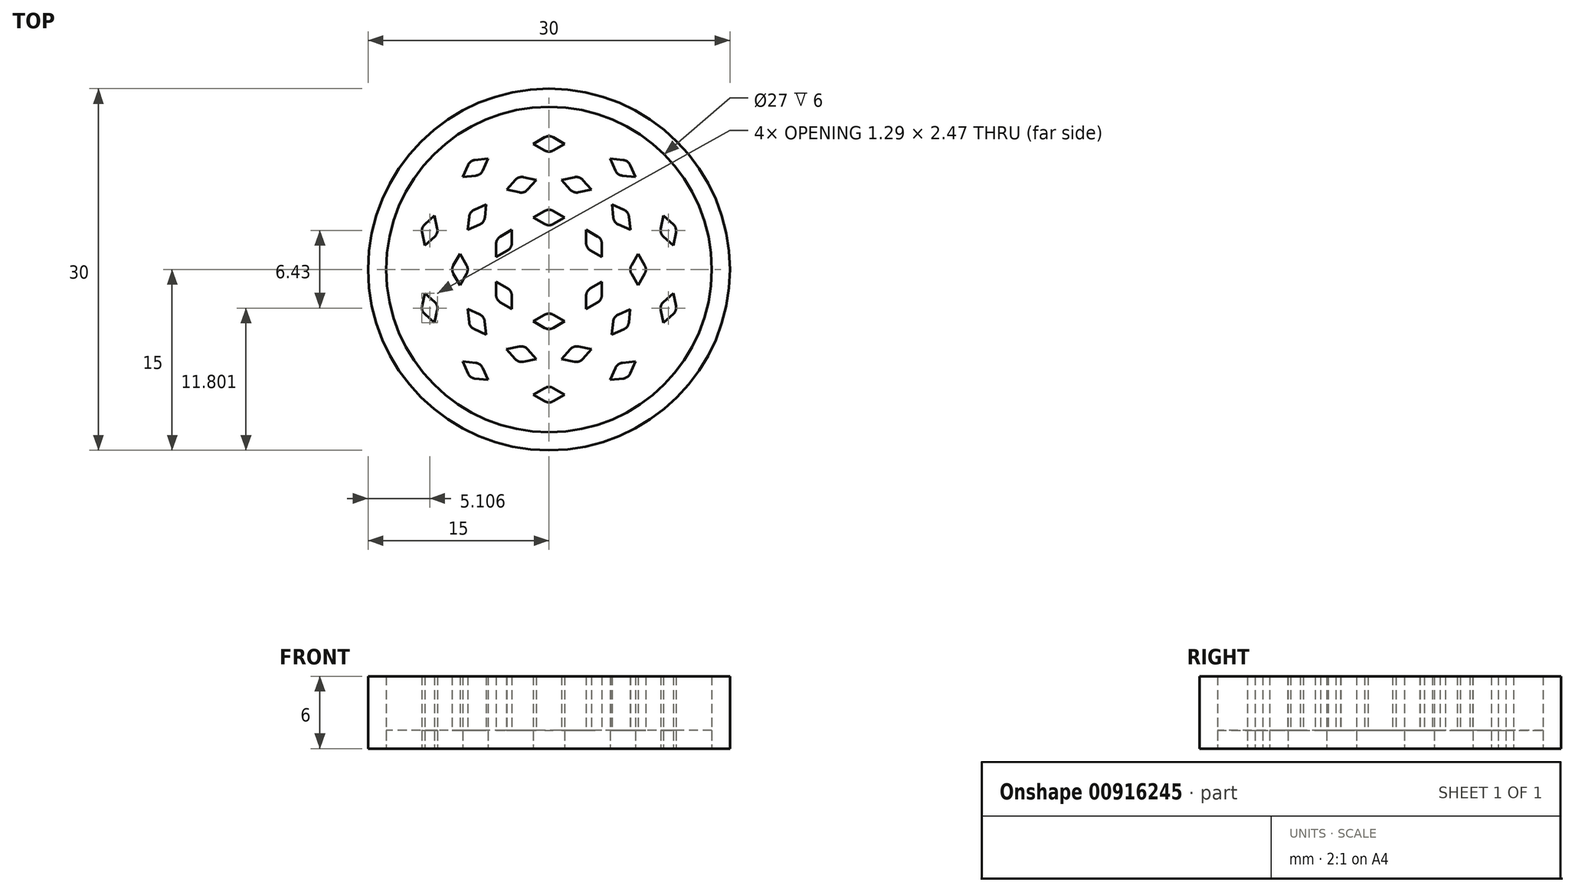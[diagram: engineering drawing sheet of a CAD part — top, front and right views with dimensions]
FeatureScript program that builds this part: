
annotation { "Feature Type Name" : "Feature", "Feature Type Description" : "" }
export const myFeature = defineFeature(function(context is Context, id is Id, definition is map)
    precondition{}
    {
        {
            var Q0;
            Q0=qCreatedBy(makeId("Top.planeOp"),FACE);
            var sketch = newSketch(context, id + "F0", { "sketchPlane" : qUnion([Q0])});
            skCircle(sketch, "E0", {"center": v(0, 0) * mm, "radius": 15 * mm});
            skCircle(sketch, "E1.0", {"center": v(0, 0) * mm, "radius": 13.5 * mm});
            skCircle(sketch, "E2.0", {"center": v(0, 0) * mm, "radius": 10.5 * mm, "construction": true});
            skCircle(sketch, "E3.0", {"center": v(0, 0) * mm, "radius": 7.5 * mm, "construction": true});
            skCircle(sketch, "E4.0", {"center": v(0, 0) * mm, "radius": 4.5 * mm, "construction": true});
            skLineSegment(sketch, "E5", {"start": v(0, 10.5) * mm, "end": v(0, 10.5) * mm});
            skLineSegment(sketch, "E6", {"start": v(0, 18.88) * mm, "end": v(0, 0) * mm, "construction": true});
            skLineSegment(sketch, "E7", {"start": v(-0.35, 10.97) * mm, "end": v(-1.3, 10.42) * mm});
            skLineSegment(sketch, "E8", {"start": v(0.35, 10.97) * mm, "end": v(1.3, 10.42) * mm});
            skPoint(sketch, "E9.visualSharp", {"position": v(0, 11.17) * mm});
            skArc(sketch, "E9.filletArc", {"start": v(0.35, 10.97) * mm, "mid": v(0, 11.06) * mm, "end": v(-0.35, 10.97) * mm});
            skLineSegment(sketch, "E10", {"start": v(-1.3, 10.42) * mm, "end": v(-0.35, 9.87) * mm});
            skLineSegment(sketch, "E11", {"start": v(0.35, 9.87) * mm, "end": v(1.3, 10.42) * mm});
            skPoint(sketch, "E12.visualSharp", {"position": v(0, 9.67) * mm});
            skArc(sketch, "E12.filletArc", {"start": v(-0.35, 9.87) * mm, "mid": v(0, 9.78) * mm, "end": v(0.35, 9.87) * mm});
            skLineSegment(sketch, "E13.1.1", {"start": v(-7.17, 7.67) * mm, "end": v(-6.08, 7.78) * mm});
            skLineSegment(sketch, "E13.1.2", {"start": v(-6.72, 8.67) * mm, "end": v(-7.17, 7.67) * mm});
            skArc(sketch, "E13.1.3", {"start": v(-6.15, 9.08) * mm, "mid": v(-6.5, 8.95) * mm, "end": v(-6.72, 8.67) * mm});
            skLineSegment(sketch, "E13.1.4", {"start": v(-6.15, 9.08) * mm, "end": v(-5.06, 9.2) * mm});
            skLineSegment(sketch, "E13.1.5", {"start": v(-5.5, 8.2) * mm, "end": v(-5.06, 9.2) * mm});
            skArc(sketch, "E13.1.6", {"start": v(-6.08, 7.78) * mm, "mid": v(-5.74, 7.91) * mm, "end": v(-5.5, 8.2) * mm});
            skCircle(sketch, "E13.2.0", {"center": v(0.02, 0.01) * mm, "radius": 10.5 * mm, "construction": true});
            skLineSegment(sketch, "E13.2.1", {"start": v(-10.3, 2) * mm, "end": v(-9.48, 2.73) * mm});
            skLineSegment(sketch, "E13.2.2", {"start": v(-10.52, 3.07) * mm, "end": v(-10.3, 2) * mm});
            skArc(sketch, "E13.2.3", {"start": v(-10.3, 3.73) * mm, "mid": v(-10.5, 3.43) * mm, "end": v(-10.52, 3.07) * mm});
            skLineSegment(sketch, "E13.2.4", {"start": v(-10.3, 3.73) * mm, "end": v(-9.5, 4.47) * mm});
            skLineSegment(sketch, "E13.2.5", {"start": v(-9.26, 3.4) * mm, "end": v(-9.5, 4.47) * mm});
            skArc(sketch, "E13.2.6", {"start": v(-9.48, 2.73) * mm, "mid": v(-9.28, 3.03) * mm, "end": v(-9.26, 3.4) * mm});
            skCircle(sketch, "E13.3.0", {"center": v(0.02, 0.02) * mm, "radius": 10.5 * mm, "construction": true});
            skLineSegment(sketch, "E13.3.1", {"start": v(-9.5, -4.43) * mm, "end": v(-9.26, -3.36) * mm});
            skLineSegment(sketch, "E13.3.2", {"start": v(-10.3, -3.7) * mm, "end": v(-9.5, -4.43) * mm});
            skArc(sketch, "E13.3.3", {"start": v(-10.52, -3.04) * mm, "mid": v(-10.5, -3.4) * mm, "end": v(-10.3, -3.7) * mm});
            skLineSegment(sketch, "E13.3.4", {"start": v(-10.52, -3.04) * mm, "end": v(-10.3, -1.96) * mm});
            skLineSegment(sketch, "E13.3.5", {"start": v(-9.48, -2.7) * mm, "end": v(-10.3, -1.96) * mm});
            skArc(sketch, "E13.3.6", {"start": v(-9.26, -3.36) * mm, "mid": v(-9.28, -3) * mm, "end": v(-9.48, -2.7) * mm});
            skCircle(sketch, "E13.4.0", {"center": v(0, 0.03) * mm, "radius": 10.5 * mm, "construction": true});
            skLineSegment(sketch, "E13.4.1", {"start": v(-5.06, -9.16) * mm, "end": v(-5.5, -8.16) * mm});
            skLineSegment(sketch, "E13.4.2", {"start": v(-6.15, -9.05) * mm, "end": v(-5.06, -9.16) * mm});
            skArc(sketch, "E13.4.3", {"start": v(-6.72, -8.64) * mm, "mid": v(-6.5, -8.92) * mm, "end": v(-6.15, -9.05) * mm});
            skLineSegment(sketch, "E13.4.4", {"start": v(-6.72, -8.64) * mm, "end": v(-7.17, -7.64) * mm});
            skLineSegment(sketch, "E13.4.5", {"start": v(-6.08, -7.75) * mm, "end": v(-7.17, -7.64) * mm});
            skArc(sketch, "E13.4.6", {"start": v(-5.5, -8.16) * mm, "mid": v(-5.74, -7.88) * mm, "end": v(-6.08, -7.75) * mm});
            skCircle(sketch, "E13.5.0", {"center": v(0, 0.03) * mm, "radius": 10.5 * mm, "construction": true});
            skLineSegment(sketch, "E13.5.1", {"start": v(1.3, -10.39) * mm, "end": v(0.35, -9.84) * mm});
            skLineSegment(sketch, "E13.5.2", {"start": v(0.35, -10.94) * mm, "end": v(1.3, -10.39) * mm});
            skArc(sketch, "E13.5.3", {"start": v(-0.35, -10.94) * mm, "mid": v(0, -11.03) * mm, "end": v(0.35, -10.94) * mm});
            skLineSegment(sketch, "E13.5.4", {"start": v(-0.35, -10.94) * mm, "end": v(-1.3, -10.39) * mm});
            skLineSegment(sketch, "E13.5.5", {"start": v(-0.35, -9.84) * mm, "end": v(-1.3, -10.39) * mm});
            skArc(sketch, "E13.5.6", {"start": v(0.35, -9.84) * mm, "mid": v(0, -9.75) * mm, "end": v(-0.35, -9.84) * mm});
            skCircle(sketch, "E13.6.0", {"center": v(0, 0.03) * mm, "radius": 10.5 * mm, "construction": true});
            skLineSegment(sketch, "E13.6.1", {"start": v(7.17, -7.64) * mm, "end": v(6.08, -7.75) * mm});
            skLineSegment(sketch, "E13.6.2", {"start": v(6.72, -8.64) * mm, "end": v(7.17, -7.64) * mm});
            skArc(sketch, "E13.6.3", {"start": v(6.15, -9.05) * mm, "mid": v(6.5, -8.92) * mm, "end": v(6.72, -8.64) * mm});
            skLineSegment(sketch, "E13.6.4", {"start": v(6.15, -9.05) * mm, "end": v(5.06, -9.16) * mm});
            skLineSegment(sketch, "E13.6.5", {"start": v(5.5, -8.16) * mm, "end": v(5.06, -9.16) * mm});
            skArc(sketch, "E13.6.6", {"start": v(6.08, -7.75) * mm, "mid": v(5.74, -7.88) * mm, "end": v(5.5, -8.16) * mm});
            skCircle(sketch, "E13.7.0", {"center": v(-0.02, 0.02) * mm, "radius": 10.5 * mm, "construction": true});
            skLineSegment(sketch, "E13.7.1", {"start": v(10.3, -1.96) * mm, "end": v(9.48, -2.7) * mm});
            skLineSegment(sketch, "E13.7.2", {"start": v(10.52, -3.04) * mm, "end": v(10.3, -1.96) * mm});
            skArc(sketch, "E13.7.3", {"start": v(10.3, -3.7) * mm, "mid": v(10.5, -3.4) * mm, "end": v(10.52, -3.04) * mm});
            skLineSegment(sketch, "E13.7.4", {"start": v(10.3, -3.7) * mm, "end": v(9.5, -4.43) * mm});
            skLineSegment(sketch, "E13.7.5", {"start": v(9.26, -3.36) * mm, "end": v(9.5, -4.43) * mm});
            skArc(sketch, "E13.7.6", {"start": v(9.48, -2.7) * mm, "mid": v(9.28, -3) * mm, "end": v(9.26, -3.36) * mm});
            skCircle(sketch, "E13.8.0", {"center": v(-0.02, 0.01) * mm, "radius": 10.5 * mm, "construction": true});
            skLineSegment(sketch, "E13.8.1", {"start": v(9.5, 4.47) * mm, "end": v(9.26, 3.4) * mm});
            skLineSegment(sketch, "E13.8.2", {"start": v(10.3, 3.73) * mm, "end": v(9.5, 4.47) * mm});
            skArc(sketch, "E13.8.3", {"start": v(10.52, 3.07) * mm, "mid": v(10.5, 3.43) * mm, "end": v(10.3, 3.73) * mm});
            skLineSegment(sketch, "E13.8.4", {"start": v(10.52, 3.07) * mm, "end": v(10.3, 2) * mm});
            skLineSegment(sketch, "E13.8.5", {"start": v(9.48, 2.73) * mm, "end": v(10.3, 2) * mm});
            skArc(sketch, "E13.8.6", {"start": v(9.26, 3.4) * mm, "mid": v(9.28, 3.03) * mm, "end": v(9.48, 2.73) * mm});
            skLineSegment(sketch, "E13.9.1", {"start": v(5.06, 9.2) * mm, "end": v(5.5, 8.2) * mm});
            skLineSegment(sketch, "E13.9.2", {"start": v(6.15, 9.08) * mm, "end": v(5.06, 9.2) * mm});
            skArc(sketch, "E13.9.3", {"start": v(6.72, 8.67) * mm, "mid": v(6.5, 8.95) * mm, "end": v(6.15, 9.08) * mm});
            skLineSegment(sketch, "E13.9.4", {"start": v(6.72, 8.67) * mm, "end": v(7.17, 7.67) * mm});
            skLineSegment(sketch, "E13.9.5", {"start": v(6.08, 7.78) * mm, "end": v(7.17, 7.67) * mm});
            skArc(sketch, "E13.9.6", {"start": v(5.5, 8.2) * mm, "mid": v(5.74, 7.91) * mm, "end": v(6.08, 7.78) * mm});
            skPoint(sketch, "E13.center", {"position": v(0, 0.02) * mm});
            skLineSegment(sketch, "E14", {"start": v(-1.3, 10.42) * mm, "end": v(-5.06, 9.2) * mm, "construction": true});
            skLineSegment(sketch, "E15", {"start": v(-3.18, 9.8) * mm, "end": v(-2.31, 7.13) * mm, "construction": true});
            skLineSegment(sketch, "E16", {"start": v(-3.51, 6.63) * mm, "end": v(-2.78, 7.44) * mm});
            skLineSegment(sketch, "E17", {"start": v(-2.11, 7.66) * mm, "end": v(-1.04, 7.43) * mm});
            skLineSegment(sketch, "E18", {"start": v(-1.04, 7.43) * mm, "end": v(-1.78, 6.61) * mm});
            skLineSegment(sketch, "E19", {"start": v(-2.44, 6.4) * mm, "end": v(-3.51, 6.63) * mm});
            skPoint(sketch, "E20.visualSharp", {"position": v(-2.5, 7.74) * mm});
            skArc(sketch, "E20.filletArc", {"start": v(-2.11, 7.66) * mm, "mid": v(-2.48, 7.64) * mm, "end": v(-2.78, 7.44) * mm});
            skPoint(sketch, "E21.visualSharp", {"position": v(-2.05, 6.31) * mm});
            skArc(sketch, "E21.filletArc", {"start": v(-2.44, 6.4) * mm, "mid": v(-2.08, 6.42) * mm, "end": v(-1.78, 6.61) * mm});
            skLineSegment(sketch, "E22.1.1", {"start": v(-6.21, 4.95) * mm, "end": v(-5.2, 5.4) * mm});
            skArc(sketch, "E22.1.2", {"start": v(-6.21, 4.95) * mm, "mid": v(-6.5, 4.72) * mm, "end": v(-6.62, 4.38) * mm});
            skLineSegment(sketch, "E22.1.3", {"start": v(-6.74, 3.3) * mm, "end": v(-6.62, 4.38) * mm});
            skLineSegment(sketch, "E22.1.4", {"start": v(-5.74, 3.74) * mm, "end": v(-6.74, 3.3) * mm});
            skArc(sketch, "E22.1.5", {"start": v(-5.74, 3.74) * mm, "mid": v(-5.45, 3.97) * mm, "end": v(-5.32, 4.3) * mm});
            skLineSegment(sketch, "E22.1.6", {"start": v(-5.2, 5.4) * mm, "end": v(-5.32, 4.3) * mm});
            skLineSegment(sketch, "E22.2.1", {"start": v(-7.93, 0.35) * mm, "end": v(-7.39, 1.3) * mm});
            skArc(sketch, "E22.2.2", {"start": v(-7.93, 0.35) * mm, "mid": v(-8.03, 0) * mm, "end": v(-7.93, -0.35) * mm});
            skLineSegment(sketch, "E22.2.3", {"start": v(-7.39, -1.3) * mm, "end": v(-7.93, -0.35) * mm});
            skLineSegment(sketch, "E22.2.4", {"start": v(-6.84, -0.35) * mm, "end": v(-7.39, -1.3) * mm});
            skArc(sketch, "E22.2.5", {"start": v(-6.84, -0.35) * mm, "mid": v(-6.74, 0) * mm, "end": v(-6.84, 0.35) * mm});
            skLineSegment(sketch, "E22.2.6", {"start": v(-7.39, 1.3) * mm, "end": v(-6.84, 0.35) * mm});
            skLineSegment(sketch, "E22.3.1", {"start": v(-6.63, -4.38) * mm, "end": v(-6.74, -3.29) * mm});
            skArc(sketch, "E22.3.2", {"start": v(-6.63, -4.38) * mm, "mid": v(-6.5, -4.72) * mm, "end": v(-6.22, -4.94) * mm});
            skLineSegment(sketch, "E22.3.3", {"start": v(-5.22, -5.39) * mm, "end": v(-6.22, -4.94) * mm});
            skLineSegment(sketch, "E22.3.4", {"start": v(-5.33, -4.3) * mm, "end": v(-5.22, -5.39) * mm});
            skArc(sketch, "E22.3.5", {"start": v(-5.33, -4.3) * mm, "mid": v(-5.46, -3.96) * mm, "end": v(-5.74, -3.73) * mm});
            skLineSegment(sketch, "E22.3.6", {"start": v(-6.74, -3.29) * mm, "end": v(-5.74, -3.73) * mm});
            skLineSegment(sketch, "E22.4.1", {"start": v(-2.79, -7.44) * mm, "end": v(-3.52, -6.62) * mm});
            skArc(sketch, "E22.4.2", {"start": v(-2.79, -7.44) * mm, "mid": v(-2.49, -7.63) * mm, "end": v(-2.12, -7.65) * mm});
            skLineSegment(sketch, "E22.4.3", {"start": v(-1.05, -7.43) * mm, "end": v(-2.12, -7.65) * mm});
            skLineSegment(sketch, "E22.4.4", {"start": v(-1.78, -6.61) * mm, "end": v(-1.05, -7.43) * mm});
            skArc(sketch, "E22.4.5", {"start": v(-1.78, -6.61) * mm, "mid": v(-2.09, -6.41) * mm, "end": v(-2.45, -6.4) * mm});
            skLineSegment(sketch, "E22.4.6", {"start": v(-3.52, -6.62) * mm, "end": v(-2.45, -6.4) * mm});
            skLineSegment(sketch, "E22.5.1", {"start": v(2.11, -7.66) * mm, "end": v(1.04, -7.43) * mm});
            skArc(sketch, "E22.5.2", {"start": v(2.11, -7.66) * mm, "mid": v(2.48, -7.64) * mm, "end": v(2.78, -7.44) * mm});
            skLineSegment(sketch, "E22.5.3", {"start": v(3.51, -6.63) * mm, "end": v(2.78, -7.44) * mm});
            skLineSegment(sketch, "E22.5.4", {"start": v(2.44, -6.4) * mm, "end": v(3.51, -6.63) * mm});
            skArc(sketch, "E22.5.5", {"start": v(2.44, -6.4) * mm, "mid": v(2.08, -6.42) * mm, "end": v(1.78, -6.61) * mm});
            skLineSegment(sketch, "E22.5.6", {"start": v(1.04, -7.43) * mm, "end": v(1.78, -6.61) * mm});
            skLineSegment(sketch, "E22.6.1", {"start": v(6.21, -4.95) * mm, "end": v(5.2, -5.4) * mm});
            skArc(sketch, "E22.6.2", {"start": v(6.21, -4.95) * mm, "mid": v(6.5, -4.72) * mm, "end": v(6.62, -4.38) * mm});
            skLineSegment(sketch, "E22.6.3", {"start": v(6.74, -3.3) * mm, "end": v(6.62, -4.38) * mm});
            skLineSegment(sketch, "E22.6.4", {"start": v(5.74, -3.74) * mm, "end": v(6.74, -3.3) * mm});
            skArc(sketch, "E22.6.5", {"start": v(5.74, -3.74) * mm, "mid": v(5.45, -3.97) * mm, "end": v(5.32, -4.3) * mm});
            skLineSegment(sketch, "E22.6.6", {"start": v(5.2, -5.4) * mm, "end": v(5.32, -4.3) * mm});
            skLineSegment(sketch, "E22.7.1", {"start": v(7.93, -0.35) * mm, "end": v(7.39, -1.3) * mm});
            skArc(sketch, "E22.7.2", {"start": v(7.93, -0.35) * mm, "mid": v(8.03, 0) * mm, "end": v(7.93, 0.35) * mm});
            skLineSegment(sketch, "E22.7.3", {"start": v(7.39, 1.3) * mm, "end": v(7.93, 0.35) * mm});
            skLineSegment(sketch, "E22.7.4", {"start": v(6.84, 0.35) * mm, "end": v(7.39, 1.3) * mm});
            skArc(sketch, "E22.7.5", {"start": v(6.84, 0.35) * mm, "mid": v(6.74, 0) * mm, "end": v(6.84, -0.35) * mm});
            skLineSegment(sketch, "E22.7.6", {"start": v(7.39, -1.3) * mm, "end": v(6.84, -0.35) * mm});
            skLineSegment(sketch, "E22.8.1", {"start": v(6.63, 4.38) * mm, "end": v(6.74, 3.29) * mm});
            skArc(sketch, "E22.8.2", {"start": v(6.63, 4.38) * mm, "mid": v(6.5, 4.72) * mm, "end": v(6.22, 4.94) * mm});
            skLineSegment(sketch, "E22.8.3", {"start": v(5.22, 5.39) * mm, "end": v(6.22, 4.94) * mm});
            skLineSegment(sketch, "E22.8.4", {"start": v(5.33, 4.3) * mm, "end": v(5.22, 5.39) * mm});
            skArc(sketch, "E22.8.5", {"start": v(5.33, 4.3) * mm, "mid": v(5.46, 3.96) * mm, "end": v(5.74, 3.73) * mm});
            skLineSegment(sketch, "E22.8.6", {"start": v(6.74, 3.29) * mm, "end": v(5.74, 3.73) * mm});
            skLineSegment(sketch, "E22.9.1", {"start": v(2.79, 7.44) * mm, "end": v(3.52, 6.62) * mm});
            skArc(sketch, "E22.9.2", {"start": v(2.79, 7.44) * mm, "mid": v(2.49, 7.63) * mm, "end": v(2.12, 7.65) * mm});
            skLineSegment(sketch, "E22.9.3", {"start": v(1.05, 7.43) * mm, "end": v(2.12, 7.65) * mm});
            skLineSegment(sketch, "E22.9.4", {"start": v(1.78, 6.61) * mm, "end": v(1.05, 7.43) * mm});
            skArc(sketch, "E22.9.5", {"start": v(1.78, 6.61) * mm, "mid": v(2.09, 6.41) * mm, "end": v(2.45, 6.4) * mm});
            skLineSegment(sketch, "E22.9.6", {"start": v(3.52, 6.62) * mm, "end": v(2.45, 6.4) * mm});
            skLineSegment(sketch, "E23", {"start": v(-1.3, 4.3) * mm, "end": v(-0.35, 4.86) * mm});
            skLineSegment(sketch, "E24", {"start": v(0.35, 4.86) * mm, "end": v(1.3, 4.3) * mm});
            skLineSegment(sketch, "E25", {"start": v(1.3, 4.3) * mm, "end": v(0.35, 3.76) * mm});
            skLineSegment(sketch, "E26", {"start": v(-0.35, 3.76) * mm, "end": v(-1.3, 4.3) * mm});
            skPoint(sketch, "E27.visualSharp", {"position": v(0, 5.06) * mm});
            skArc(sketch, "E27.filletArc", {"start": v(0.35, 4.86) * mm, "mid": v(0, 4.95) * mm, "end": v(-0.35, 4.86) * mm});
            skPoint(sketch, "E28.visualSharp", {"position": v(0, 3.56) * mm});
            skArc(sketch, "E28.filletArc", {"start": v(-0.35, 3.76) * mm, "mid": v(0, 3.67) * mm, "end": v(0.35, 3.76) * mm});
            skLineSegment(sketch, "E29.1.1", {"start": v(-4.03, 2.73) * mm, "end": v(-3.08, 3.28) * mm});
            skArc(sketch, "E29.1.2", {"start": v(-4.03, 2.73) * mm, "mid": v(-4.29, 2.48) * mm, "end": v(-4.38, 2.13) * mm});
            skLineSegment(sketch, "E29.1.3", {"start": v(-4.38, 1.03) * mm, "end": v(-4.38, 2.13) * mm});
            skLineSegment(sketch, "E29.1.4", {"start": v(-3.43, 1.58) * mm, "end": v(-4.38, 1.03) * mm});
            skArc(sketch, "E29.1.5", {"start": v(-3.43, 1.58) * mm, "mid": v(-3.18, 1.83) * mm, "end": v(-3.08, 2.18) * mm});
            skLineSegment(sketch, "E29.1.6", {"start": v(-3.08, 3.28) * mm, "end": v(-3.08, 2.18) * mm});
            skLineSegment(sketch, "E29.2.1", {"start": v(-4.38, -2.13) * mm, "end": v(-4.38, -1.03) * mm});
            skArc(sketch, "E29.2.2", {"start": v(-4.38, -2.13) * mm, "mid": v(-4.29, -2.48) * mm, "end": v(-4.03, -2.73) * mm});
            skLineSegment(sketch, "E29.2.3", {"start": v(-3.08, -3.28) * mm, "end": v(-4.03, -2.73) * mm});
            skLineSegment(sketch, "E29.2.4", {"start": v(-3.08, -2.18) * mm, "end": v(-3.08, -3.28) * mm});
            skArc(sketch, "E29.2.5", {"start": v(-3.08, -2.18) * mm, "mid": v(-3.18, -1.83) * mm, "end": v(-3.43, -1.58) * mm});
            skLineSegment(sketch, "E29.2.6", {"start": v(-4.38, -1.03) * mm, "end": v(-3.43, -1.58) * mm});
            skLineSegment(sketch, "E29.3.1", {"start": v(-0.35, -4.86) * mm, "end": v(-1.3, -4.3) * mm});
            skArc(sketch, "E29.3.2", {"start": v(-0.35, -4.86) * mm, "mid": v(0, -4.95) * mm, "end": v(0.35, -4.86) * mm});
            skLineSegment(sketch, "E29.3.3", {"start": v(1.3, -4.3) * mm, "end": v(0.35, -4.86) * mm});
            skLineSegment(sketch, "E29.3.4", {"start": v(0.35, -3.76) * mm, "end": v(1.3, -4.3) * mm});
            skArc(sketch, "E29.3.5", {"start": v(0.35, -3.76) * mm, "mid": v(0, -3.67) * mm, "end": v(-0.35, -3.76) * mm});
            skLineSegment(sketch, "E29.3.6", {"start": v(-1.3, -4.3) * mm, "end": v(-0.35, -3.76) * mm});
            skLineSegment(sketch, "E29.4.1", {"start": v(4.03, -2.73) * mm, "end": v(3.08, -3.28) * mm});
            skArc(sketch, "E29.4.2", {"start": v(4.03, -2.73) * mm, "mid": v(4.29, -2.48) * mm, "end": v(4.38, -2.13) * mm});
            skLineSegment(sketch, "E29.4.3", {"start": v(4.38, -1.03) * mm, "end": v(4.38, -2.13) * mm});
            skLineSegment(sketch, "E29.4.4", {"start": v(3.43, -1.58) * mm, "end": v(4.38, -1.03) * mm});
            skArc(sketch, "E29.4.5", {"start": v(3.43, -1.58) * mm, "mid": v(3.18, -1.83) * mm, "end": v(3.08, -2.18) * mm});
            skLineSegment(sketch, "E29.4.6", {"start": v(3.08, -3.28) * mm, "end": v(3.08, -2.18) * mm});
            skLineSegment(sketch, "E29.5.1", {"start": v(4.38, 2.13) * mm, "end": v(4.38, 1.03) * mm});
            skArc(sketch, "E29.5.2", {"start": v(4.38, 2.13) * mm, "mid": v(4.29, 2.48) * mm, "end": v(4.03, 2.73) * mm});
            skLineSegment(sketch, "E29.5.3", {"start": v(3.08, 3.28) * mm, "end": v(4.03, 2.73) * mm});
            skLineSegment(sketch, "E29.5.4", {"start": v(3.08, 2.18) * mm, "end": v(3.08, 3.28) * mm});
            skArc(sketch, "E29.5.5", {"start": v(3.08, 2.18) * mm, "mid": v(3.18, 1.83) * mm, "end": v(3.43, 1.58) * mm});
            skLineSegment(sketch, "E29.5.6", {"start": v(4.38, 1.03) * mm, "end": v(3.43, 1.58) * mm});
            skSolve(sketch);
        }
        {
            var Q0;
            Q0=makeQuery(id+"F0.imprint","IMPRINT",FACE,{"disambiguationData":[TD([[makeQuery(id+"F0.imprint","IMPRINT",EDGE,{"derivedFrom":sQuery(id+"F0.wireOp",EDGE,"E13.1.1")}),1.0]])]});
            var Q1;
            Q1=makeQuery(id+"F0.imprint","IMPRINT",FACE,{"disambiguationData":[TD([[makeQuery(id+"F0.imprint","IMPRINT",EDGE,{"derivedFrom":sQuery(id+"F0.wireOp",EDGE,"E7")}),1.0]])]});
            var Q2;
            Q2=makeQuery(id+"F0.imprint","IMPRINT",FACE,{"disambiguationData":[TD([[makeQuery(id+"F0.imprint","IMPRINT",EDGE,{"derivedFrom":sQuery(id+"F0.wireOp",EDGE,"E13.9.1")}),1.0]])]});
            var Q3;
            Q3=makeQuery(id+"F0.imprint","IMPRINT",FACE,{"disambiguationData":[TD([[makeQuery(id+"F0.imprint","IMPRINT",EDGE,{"derivedFrom":sQuery(id+"F0.wireOp",EDGE,"E13.8.1")}),1.0]])]});
            var Q4;
            Q4=makeQuery(id+"F0.imprint","IMPRINT",FACE,{"disambiguationData":[TD([[makeQuery(id+"F0.imprint","IMPRINT",EDGE,{"derivedFrom":sQuery(id+"F0.wireOp",EDGE,"E13.7.1")}),1.0]])]});
            var Q5;
            Q5=makeQuery(id+"F0.imprint","IMPRINT",FACE,{"disambiguationData":[TD([[makeQuery(id+"F0.imprint","IMPRINT",EDGE,{"derivedFrom":sQuery(id+"F0.wireOp",EDGE,"E13.6.1")}),1.0]])]});
            var Q6;
            Q6=makeQuery(id+"F0.imprint","IMPRINT",FACE,{"disambiguationData":[TD([[makeQuery(id+"F0.imprint","IMPRINT",EDGE,{"derivedFrom":sQuery(id+"F0.wireOp",EDGE,"E13.5.1")}),1.0]])]});
            var Q7;
            Q7=makeQuery(id+"F0.imprint","IMPRINT",FACE,{"disambiguationData":[TD([[makeQuery(id+"F0.imprint","IMPRINT",EDGE,{"derivedFrom":sQuery(id+"F0.wireOp",EDGE,"E13.4.1")}),1.0]])]});
            var Q8;
            Q8=makeQuery(id+"F0.imprint","IMPRINT",FACE,{"disambiguationData":[TD([[makeQuery(id+"F0.imprint","IMPRINT",EDGE,{"derivedFrom":sQuery(id+"F0.wireOp",EDGE,"E13.3.1")}),1.0]])]});
            var Q9;
            Q9=makeQuery(id+"F0.imprint","IMPRINT",FACE,{"disambiguationData":[TD([[makeQuery(id+"F0.imprint","IMPRINT",EDGE,{"derivedFrom":sQuery(id+"F0.wireOp",EDGE,"E13.2.1")}),1.0]])]});
            extrude(context, id + "F1", {"entities" : qUnion([Q0, Q1, Q2, Q3, Q4, Q5, Q6, Q7, Q8, Q9]), "depth" : 6 * mm, "offsetDistance" : 25 * mm});
        }
        {
            var Q0;
            Q0=makeQuery(id+"F0.imprint","IMPRINT",FACE,{"disambiguationData":[TD([[makeQuery(id+"F0.imprint","IMPRINT",EDGE,{"derivedFrom":sQuery(id+"F0.wireOp",EDGE,"E0")}),1.0]])]});
            extrude(context, id + "F2", {"entities" : qUnion([Q0]), "depth" : 6 * mm, "offsetDistance" : 25 * mm});
        }
        {
            var Q0;
            Q0=makeQuery(id+"F0.imprint","IMPRINT",FACE,{"disambiguationData":[TD([[makeQuery(id+"F0.imprint","IMPRINT",EDGE,{"derivedFrom":sQuery(id+"F0.wireOp",EDGE,"E1.0")}),1.0]])]});
            extrude(context, id + "F3", {"entities" : qUnion([Q0]), "depth" : 1.5 * mm, "offsetDistance" : 25 * mm});
        }
        {
            var Q0;
            Q0=makeQuery(id+"F0.imprint","IMPRINT",FACE,{"disambiguationData":[TD([[makeQuery(id+"F0.imprint","IMPRINT",EDGE,{"derivedFrom":sQuery(id+"F0.wireOp",EDGE,"E22.1.1")}),-1.0]])]});
            var Q1;
            Q1=makeQuery(id+"F0.imprint","IMPRINT",FACE,{"disambiguationData":[TD([[makeQuery(id+"F0.imprint","IMPRINT",EDGE,{"derivedFrom":sQuery(id+"F0.wireOp",EDGE,"E16")}),-1.0]])]});
            var Q2;
            Q2=makeQuery(id+"F0.imprint","IMPRINT",FACE,{"disambiguationData":[TD([[makeQuery(id+"F0.imprint","IMPRINT",EDGE,{"derivedFrom":sQuery(id+"F0.wireOp",EDGE,"E22.9.1")}),-1.0]])]});
            var Q3;
            Q3=makeQuery(id+"F0.imprint","IMPRINT",FACE,{"disambiguationData":[TD([[makeQuery(id+"F0.imprint","IMPRINT",EDGE,{"derivedFrom":sQuery(id+"F0.wireOp",EDGE,"E23")}),-1.0]])]});
            var Q4;
            Q4=makeQuery(id+"F0.imprint","IMPRINT",FACE,{"disambiguationData":[TD([[makeQuery(id+"F0.imprint","IMPRINT",EDGE,{"derivedFrom":sQuery(id+"F0.wireOp",EDGE,"E29.1.1")}),-1.0]])]});
            var Q5;
            Q5=makeQuery(id+"F0.imprint","IMPRINT",FACE,{"disambiguationData":[TD([[makeQuery(id+"F0.imprint","IMPRINT",EDGE,{"derivedFrom":sQuery(id+"F0.wireOp",EDGE,"E22.2.1")}),-1.0]])]});
            var Q6;
            Q6=makeQuery(id+"F0.imprint","IMPRINT",FACE,{"disambiguationData":[TD([[makeQuery(id+"F0.imprint","IMPRINT",EDGE,{"derivedFrom":sQuery(id+"F0.wireOp",EDGE,"E29.5.1")}),-1.0]])]});
            var Q7;
            Q7=makeQuery(id+"F0.imprint","IMPRINT",FACE,{"disambiguationData":[TD([[makeQuery(id+"F0.imprint","IMPRINT",EDGE,{"derivedFrom":sQuery(id+"F0.wireOp",EDGE,"E22.8.1")}),-1.0]])]});
            var Q8;
            Q8=makeQuery(id+"F0.imprint","IMPRINT",FACE,{"disambiguationData":[TD([[makeQuery(id+"F0.imprint","IMPRINT",EDGE,{"derivedFrom":sQuery(id+"F0.wireOp",EDGE,"E29.4.1")}),-1.0]])]});
            var Q9;
            Q9=makeQuery(id+"F0.imprint","IMPRINT",FACE,{"disambiguationData":[TD([[makeQuery(id+"F0.imprint","IMPRINT",EDGE,{"derivedFrom":sQuery(id+"F0.wireOp",EDGE,"E29.2.1")}),-1.0]])]});
            var Q10;
            Q10=makeQuery(id+"F0.imprint","IMPRINT",FACE,{"disambiguationData":[TD([[makeQuery(id+"F0.imprint","IMPRINT",EDGE,{"derivedFrom":sQuery(id+"F0.wireOp",EDGE,"E22.7.1")}),-1.0]])]});
            var Q11;
            Q11=makeQuery(id+"F0.imprint","IMPRINT",FACE,{"disambiguationData":[TD([[makeQuery(id+"F0.imprint","IMPRINT",EDGE,{"derivedFrom":sQuery(id+"F0.wireOp",EDGE,"E22.6.1")}),-1.0]])]});
            var Q12;
            Q12=makeQuery(id+"F0.imprint","IMPRINT",FACE,{"disambiguationData":[TD([[makeQuery(id+"F0.imprint","IMPRINT",EDGE,{"derivedFrom":sQuery(id+"F0.wireOp",EDGE,"E29.3.1")}),-1.0]])]});
            var Q13;
            Q13=makeQuery(id+"F0.imprint","IMPRINT",FACE,{"disambiguationData":[TD([[makeQuery(id+"F0.imprint","IMPRINT",EDGE,{"derivedFrom":sQuery(id+"F0.wireOp",EDGE,"E22.5.1")}),-1.0]])]});
            var Q14;
            Q14=makeQuery(id+"F0.imprint","IMPRINT",FACE,{"disambiguationData":[TD([[makeQuery(id+"F0.imprint","IMPRINT",EDGE,{"derivedFrom":sQuery(id+"F0.wireOp",EDGE,"E22.4.1")}),-1.0]])]});
            var Q15;
            Q15=makeQuery(id+"F0.imprint","IMPRINT",FACE,{"disambiguationData":[TD([[makeQuery(id+"F0.imprint","IMPRINT",EDGE,{"derivedFrom":sQuery(id+"F0.wireOp",EDGE,"E22.3.1")}),-1.0]])]});
            extrude(context, id + "F4", {"entities" : qUnion([Q0, Q1, Q2, Q3, Q4, Q5, Q6, Q7, Q8, Q9, Q10, Q11, Q12, Q13, Q14, Q15]), "operationType" : NewBodyOperationType.ADD, "depth" : 6 * mm, "offsetDistance" : 25 * mm});
        }
    });
